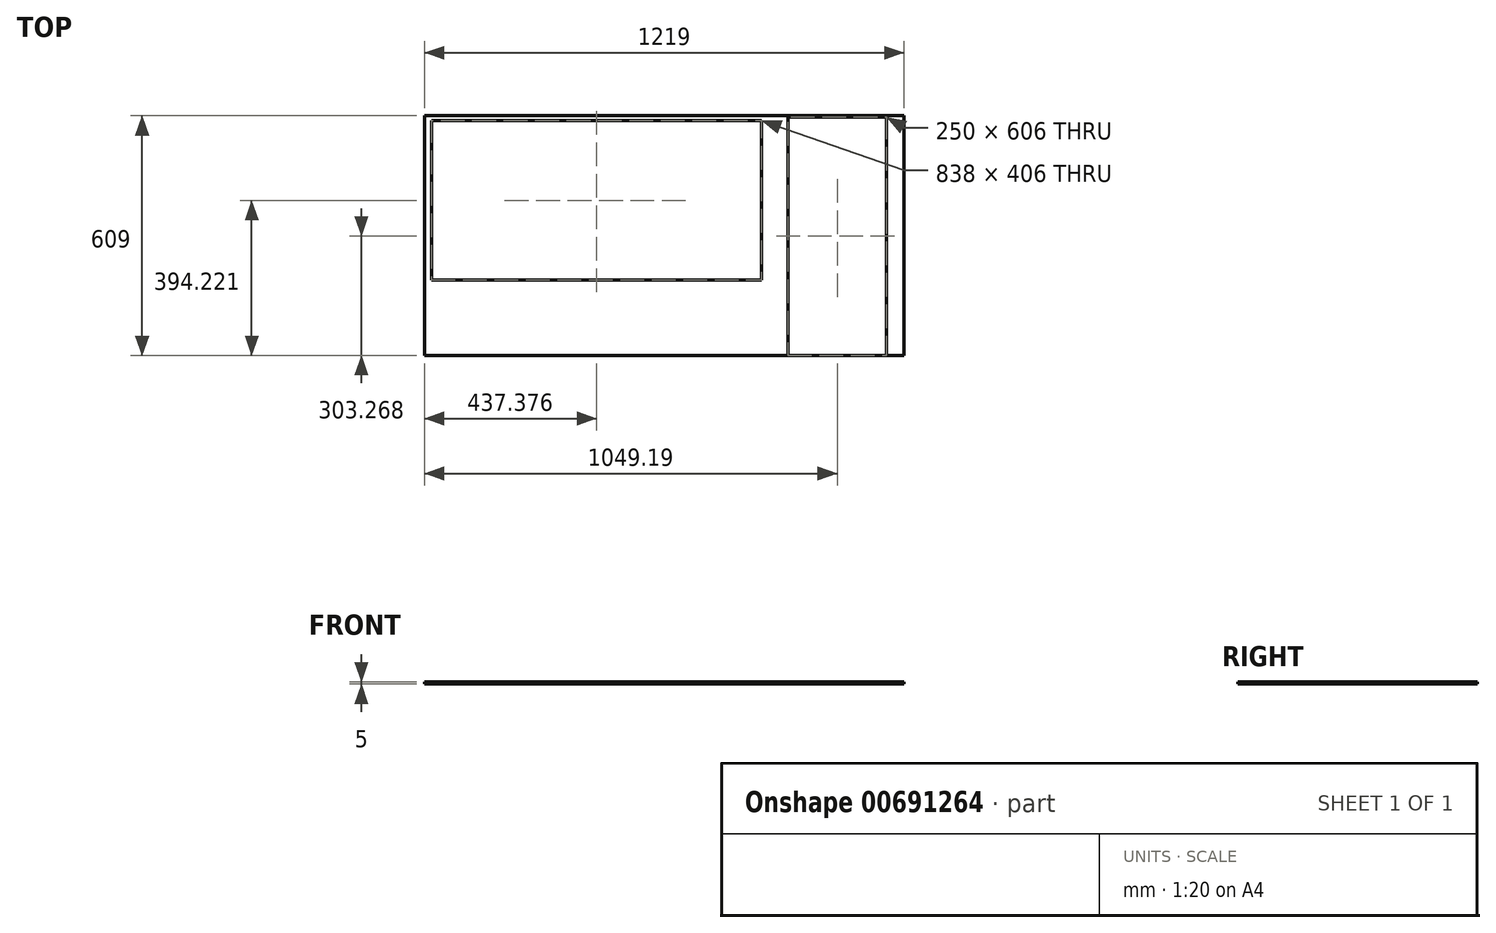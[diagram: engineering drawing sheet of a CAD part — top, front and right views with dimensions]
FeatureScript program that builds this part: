
annotation { "Feature Type Name" : "Feature", "Feature Type Description" : "" }
export const myFeature = defineFeature(function(context is Context, id is Id, definition is map)
    precondition{}
    {
        {
            var Q0;
            Q0=qCreatedBy(makeId("Top.planeOp"),FACE);
            var sketch = newSketch(context, id + "F0", { "sketchPlane" : qUnion([Q0])});
            skLineSegment(sketch, "E0.bottom", {"start": v(-609.5, 304.5) * mm, "end": v(609.5, 304.5) * mm});
            skLineSegment(sketch, "E0.top", {"start": v(-609.5, -304.5) * mm, "end": v(609.5, -304.5) * mm});
            skLineSegment(sketch, "E0.left", {"start": v(-609.5, 304.5) * mm, "end": v(-609.5, -304.5) * mm});
            skLineSegment(sketch, "E0.right", {"start": v(609.5, 304.5) * mm, "end": v(609.5, -304.5) * mm});
            skLineSegment(sketch, "E1.bottom", {"start": v(-591.12, 292.72) * mm, "end": v(246.88, 292.72) * mm});
            skLineSegment(sketch, "E1.top", {"start": v(-591.12, -113.28) * mm, "end": v(246.88, -113.28) * mm});
            skLineSegment(sketch, "E1.left", {"start": v(-591.12, 292.72) * mm, "end": v(-591.12, -113.28) * mm});
            skLineSegment(sketch, "E1.right", {"start": v(246.88, 292.72) * mm, "end": v(246.88, -113.28) * mm});
            skLineSegment(sketch, "E2.bottom", {"start": v(314.7, 301.77) * mm, "end": v(564.7, 301.77) * mm});
            skLineSegment(sketch, "E2.top", {"start": v(314.7, -304.23) * mm, "end": v(564.7, -304.23) * mm});
            skLineSegment(sketch, "E2.left", {"start": v(314.7, 301.77) * mm, "end": v(314.7, -304.23) * mm});
            skLineSegment(sketch, "E2.right", {"start": v(564.7, 301.77) * mm, "end": v(564.7, -304.23) * mm});
            skSolve(sketch);
        }
        {
            var Q0;
            Q0 = qSketchRegion(id + "F0", true);
            extrude(context, id + "F1", {"entities" : qUnion([Q0]), "depth" : 5 * mm, "offsetDistance" : 25 * mm});
        }
    });
